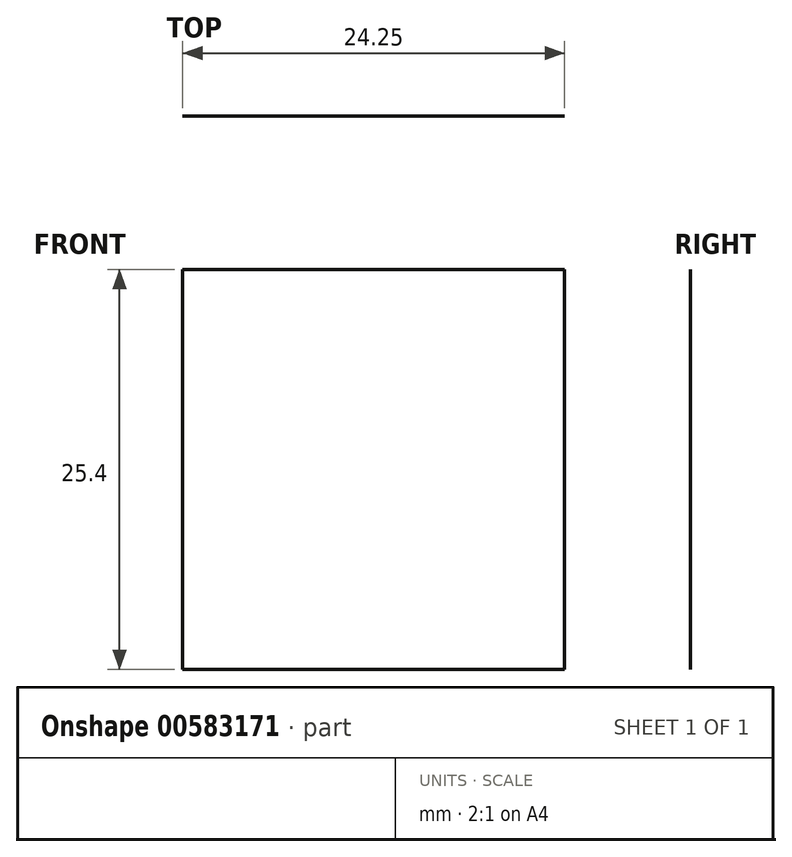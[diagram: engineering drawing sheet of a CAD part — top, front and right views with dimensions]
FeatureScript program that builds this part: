
annotation { "Feature Type Name" : "Feature", "Feature Type Description" : "" }
export const myFeature = defineFeature(function(context is Context, id is Id, definition is map)
    precondition{}
    {
        {
            var Q0;
            Q0=qCreatedBy(makeId("Top.planeOp"),FACE);
            var sketch = newSketch(context, id + "F0", { "sketchPlane" : qUnion([Q0])});
            skLineSegment(sketch, "E0.bottom", {"start": v(-203.2, 189.34) * mm, "end": v(0, 189.34) * mm});
            skLineSegment(sketch, "E0.top", {"start": v(-203.2, -13.86) * mm, "end": v(0, -13.86) * mm});
            skLineSegment(sketch, "E0.left", {"start": v(-203.2, 189.34) * mm, "end": v(-203.2, -13.86) * mm});
            skLineSegment(sketch, "E0.right", {"start": v(0, 189.34) * mm, "end": v(0, -13.86) * mm});
            skText(sketch, "E1", { "text": "A\n", "fontName": "OpenSans-Regular.ttf"});
            const initialGuessF0  = {"E1": [-0.2032, -0.01386, 1, 0, 0.2032]};
            skSetInitialGuess(sketch, initialGuessF0);
            skSolve(sketch);
        }
        {
            var Q0;
            Q0=makeQuery(id+"F0.imprint","IMPRINT",FACE,{"disambiguationData":[TD([[makeQuery(id+"F0.imprint","IMPRINT",EDGE,{"derivedFrom":sQuery(id+"F0.wireOp",EDGE,"E1.sketch_text.stroke-0")}),-1.0]])]});
            extrude(context, id + "F1", {"entities" : qUnion([Q0]), "depth" : 25.4 * mm, "offsetDistance" : 25.4 * mm});
        }
    });
